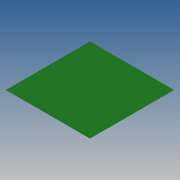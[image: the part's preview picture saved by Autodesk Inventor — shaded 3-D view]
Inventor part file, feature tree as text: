
AUTODESK INVENTOR PART (.ipt)
format: ipt  version: 2013 (Build 170138000, 138)  size: 74,240 bytes
history: native  units: in
note: dims shown in document units (in); Inventor stores cm internally (conversion verified against a paired STEP export)
features: extrude x2, sketch x2
ambient origin geometry x8: Origin, YZ Plane, XZ Plane, XY Plane, X Axis, Y Axis, Z Axis, Center Point
bodies: Solid1 (feature_tree)
feature tree (4):
  extrude  "Extrusion1"  Depth=1200.0in
  extrude  "Extrusion2"  Depth=1.0in
  sketch  "Sketch1"  dims[d0=1200.0in d1=1200.0in]
  sketch  "Sketch2"  dims[d2=1.0in d3=0.0in d4=1.0in d6=1.0in d7=0.0in]
